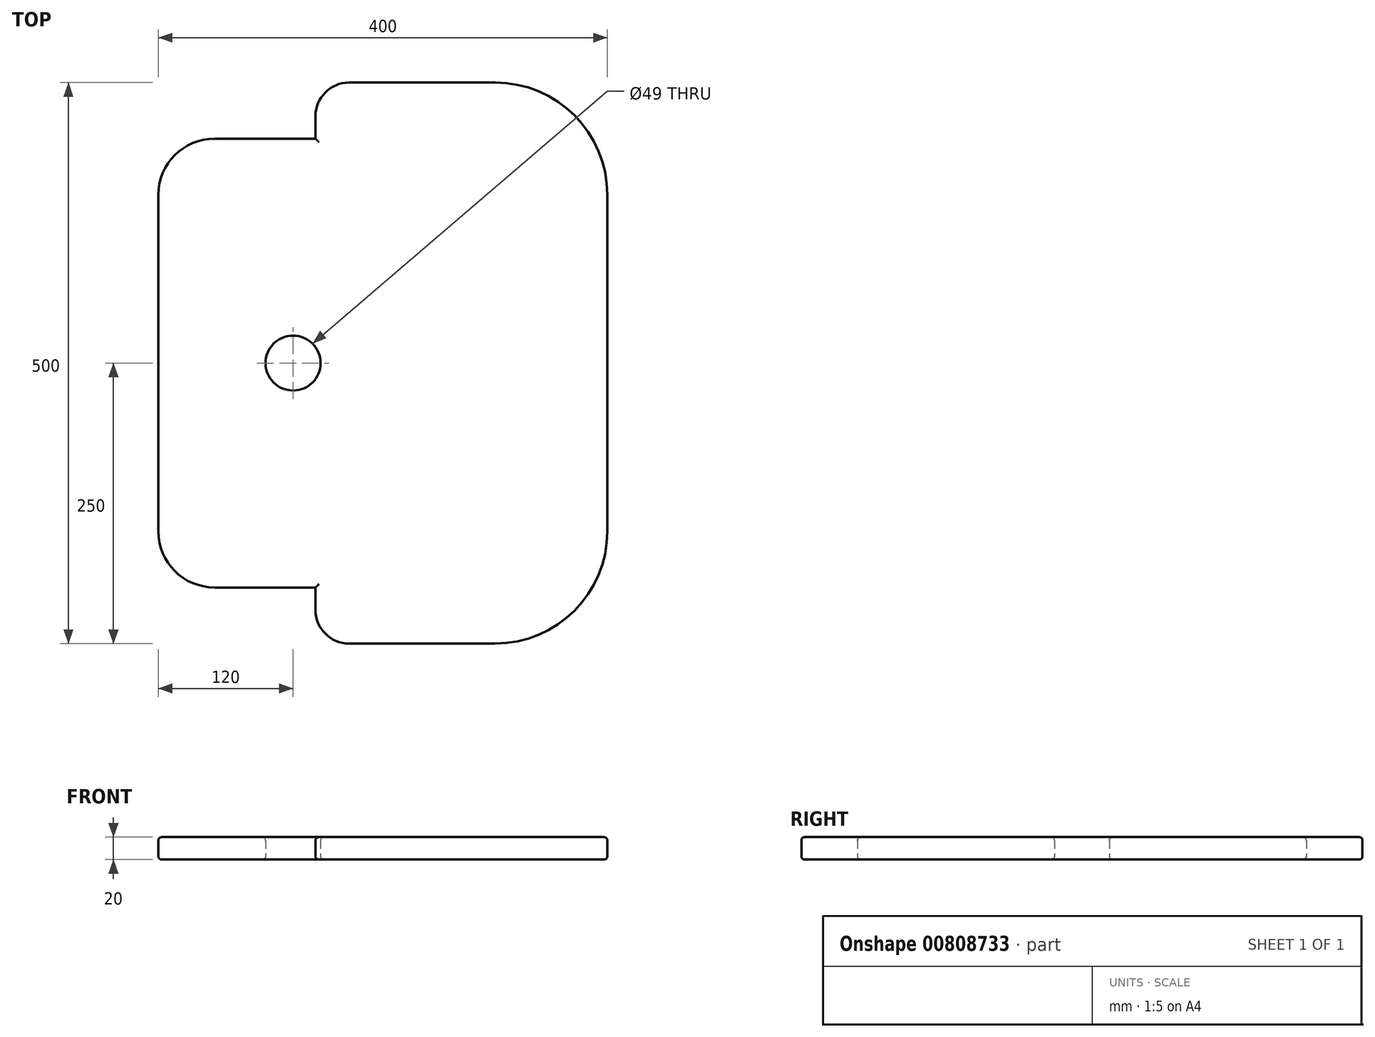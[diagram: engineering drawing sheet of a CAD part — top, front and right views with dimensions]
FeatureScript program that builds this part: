
annotation { "Feature Type Name" : "Feature", "Feature Type Description" : "" }
export const myFeature = defineFeature(function(context is Context, id is Id, definition is map)
    precondition{}
    {
        {
            var Q0;
            Q0=qCreatedBy(makeId("Top.planeOp"),FACE);
            var sketch = newSketch(context, id + "F0", { "sketchPlane" : qUnion([Q0])});
            skLineSegment(sketch, "E0.bottom", {"start": v(100, -250) * mm, "end": v(-30, -250) * mm});
            skLineSegment(sketch, "E0.top", {"start": v(100, 250) * mm, "end": v(-30, 250) * mm});
            skLineSegment(sketch, "E0.left", {"start": v(200, -150) * mm, "end": v(200, 150) * mm});
            skLineSegment(sketch, "E0.right", {"start": v(-200, -150) * mm, "end": v(-200, 150) * mm});
            skPoint(sketch, "E0.middle", {"position": v(0, 0) * mm});
            skPoint(sketch, "E1.visualSharp", {"position": v(200, 250) * mm});
            skArc(sketch, "E1.filletArc", {"start": v(200, 150) * mm, "mid": v(170.71, 220.71) * mm, "end": v(100, 250) * mm});
            skPoint(sketch, "E2.visualSharp", {"position": v(200, -250) * mm});
            skArc(sketch, "E2.filletArc", {"start": v(100, -250) * mm, "mid": v(170.71, -220.71) * mm, "end": v(200, -150) * mm});
            skLineSegment(sketch, "E3", {"start": v(-150, 200) * mm, "end": v(-60, 200) * mm});
            skLineSegment(sketch, "E4", {"start": v(-60, 200) * mm, "end": v(-60, 220) * mm});
            skLineSegment(sketch, "E5", {"start": v(-150, -200) * mm, "end": v(-60, -200) * mm});
            skLineSegment(sketch, "E6", {"start": v(-60, -200) * mm, "end": v(-60, -220) * mm});
            skPoint(sketch, "E7.end.orphan", {"position": v(-200, 250) * mm});
            skPoint(sketch, "E8.orphan", {"position": v(-200, -250) * mm});
            skPoint(sketch, "E9.visualSharp", {"position": v(-200, 200) * mm});
            skArc(sketch, "E9.filletArc", {"start": v(-150, 200) * mm, "mid": v(-185.36, 185.36) * mm, "end": v(-200, 150) * mm});
            skPoint(sketch, "E10.visualSharp", {"position": v(-200, -200) * mm});
            skArc(sketch, "E10.filletArc", {"start": v(-200, -150) * mm, "mid": v(-185.36, -185.36) * mm, "end": v(-150, -200) * mm});
            skLineSegment(sketch, "E11", {"start": v(-200, 0) * mm, "end": v(-80, 0) * mm, "construction": true});
            skCircle(sketch, "E12", {"center": v(-80, 0) * mm, "radius": 24.5 * mm});
            skPoint(sketch, "E13.visualSharp", {"position": v(-60, 250) * mm});
            skArc(sketch, "E13.filletArc", {"start": v(-30, 250) * mm, "mid": v(-51.21, 241.21) * mm, "end": v(-60, 220) * mm});
            skPoint(sketch, "E14.visualSharp", {"position": v(-60, -250) * mm});
            skArc(sketch, "E14.filletArc", {"start": v(-60, -220) * mm, "mid": v(-51.21, -241.21) * mm, "end": v(-30, -250) * mm});
            skLineSegment(sketch, "E15", {"start": v(-80, 24.5) * mm, "end": v(-80, 40.41) * mm, "construction": true});
            skPoint(sketch, "E16", {"position": v(-80, 40.41) * mm});
            skSolve(sketch);
        }
        {
            var Q0;
            Q0=makeQuery(id+"F0.imprint","IMPRINT",FACE,{"disambiguationData":[TD([[makeQuery(id+"F0.imprint","IMPRINT",EDGE,{"derivedFrom":sQuery(id+"F0.wireOp",EDGE,"E0.bottom")}),-1.0]])]});
            extrude(context, id + "F1", {"entities" : qUnion([Q0]), "depth" : 20 * mm, "offsetDistance" : 25 * mm});
        }
        {
            var Q0;
            Q0=makeQuery(id+"F1.opExtrude","CAP_FACE",FACE,{"disambiguationData":[OSD([sQuery(id+"F0.wireOp",EDGE,"E0.bottom"),sQuery(id+"F0.wireOp",EDGE,"E0.top"),sQuery(id+"F0.wireOp",EDGE,"E0.left"),sQuery(id+"F0.wireOp",EDGE,"E0.right"),sQuery(id+"F0.wireOp",EDGE,"E1.filletArc"),sQuery(id+"F0.wireOp",EDGE,"E2.filletArc"),sQuery(id+"F0.wireOp",EDGE,"E3"),sQuery(id+"F0.wireOp",EDGE,"E4"),sQuery(id+"F0.wireOp",EDGE,"E5"),sQuery(id+"F0.wireOp",EDGE,"E6"),sQuery(id+"F0.wireOp",EDGE,"E9.filletArc"),sQuery(id+"F0.wireOp",EDGE,"E10.filletArc"),sQuery(id+"F0.wireOp",EDGE,"E12"),sQuery(id+"F0.wireOp",EDGE,"E13.filletArc"),sQuery(id+"F0.wireOp",EDGE,"E14.filletArc")])],"isStart":false});
            var Q1;
            Q1=makeQuery(id+"F1.opExtrude","CAP_FACE",FACE,{"disambiguationData":[OSD([sQuery(id+"F0.wireOp",EDGE,"E0.bottom"),sQuery(id+"F0.wireOp",EDGE,"E0.top"),sQuery(id+"F0.wireOp",EDGE,"E0.left"),sQuery(id+"F0.wireOp",EDGE,"E0.right"),sQuery(id+"F0.wireOp",EDGE,"E1.filletArc"),sQuery(id+"F0.wireOp",EDGE,"E2.filletArc"),sQuery(id+"F0.wireOp",EDGE,"E3"),sQuery(id+"F0.wireOp",EDGE,"E4"),sQuery(id+"F0.wireOp",EDGE,"E5"),sQuery(id+"F0.wireOp",EDGE,"E6"),sQuery(id+"F0.wireOp",EDGE,"E9.filletArc"),sQuery(id+"F0.wireOp",EDGE,"E10.filletArc"),sQuery(id+"F0.wireOp",EDGE,"E12"),sQuery(id+"F0.wireOp",EDGE,"E13.filletArc"),sQuery(id+"F0.wireOp",EDGE,"E14.filletArc")])],"isStart":true});
            fillet(context, id + "F2", {"entities" : qUnion([Q0, Q1]), "radius" : 3 * mm, "tangentPropagation" : true, "allowEdgeOverflow" : false});
        }
        {
            var Q0;
            Q0=makeQuery(id+"F1.opExtrude","CAP_FACE",FACE,{"disambiguationData":[OSD([sQuery(id+"F0.wireOp",EDGE,"E0.bottom"),sQuery(id+"F0.wireOp",EDGE,"E0.top"),sQuery(id+"F0.wireOp",EDGE,"E0.left"),sQuery(id+"F0.wireOp",EDGE,"E0.right"),sQuery(id+"F0.wireOp",EDGE,"E1.filletArc"),sQuery(id+"F0.wireOp",EDGE,"E2.filletArc"),sQuery(id+"F0.wireOp",EDGE,"E3"),sQuery(id+"F0.wireOp",EDGE,"E4"),sQuery(id+"F0.wireOp",EDGE,"E5"),sQuery(id+"F0.wireOp",EDGE,"E6"),sQuery(id+"F0.wireOp",EDGE,"E9.filletArc"),sQuery(id+"F0.wireOp",EDGE,"E10.filletArc"),sQuery(id+"F0.wireOp",EDGE,"E12"),sQuery(id+"F0.wireOp",EDGE,"E13.filletArc"),sQuery(id+"F0.wireOp",EDGE,"E14.filletArc")])],"isStart":false});
            var sketch = newSketch(context, id + "F3", { "sketchPlane" : qUnion([Q0])});
            skLineSegment(sketch, "E17.0", {"start": v(-60, 200) * mm, "end": v(-60, 218) * mm});
            skPoint(sketch, "E18.end.orphan", {"position": v(-60, 220) * mm});
            skLineSegment(sketch, "E19", {"start": v(-60, 209) * mm, "end": v(40, 209) * mm, "construction": true});
            skPoint(sketch, "E20", {"position": v(40, 209) * mm});
            skPoint(sketch, "E21.MirrorP", {"position": v(40, -209) * mm});
            skPoint(sketch, "E22.0", {"position": v(-80, 40.41) * mm});
            skSolve(sketch);
        }
    });
